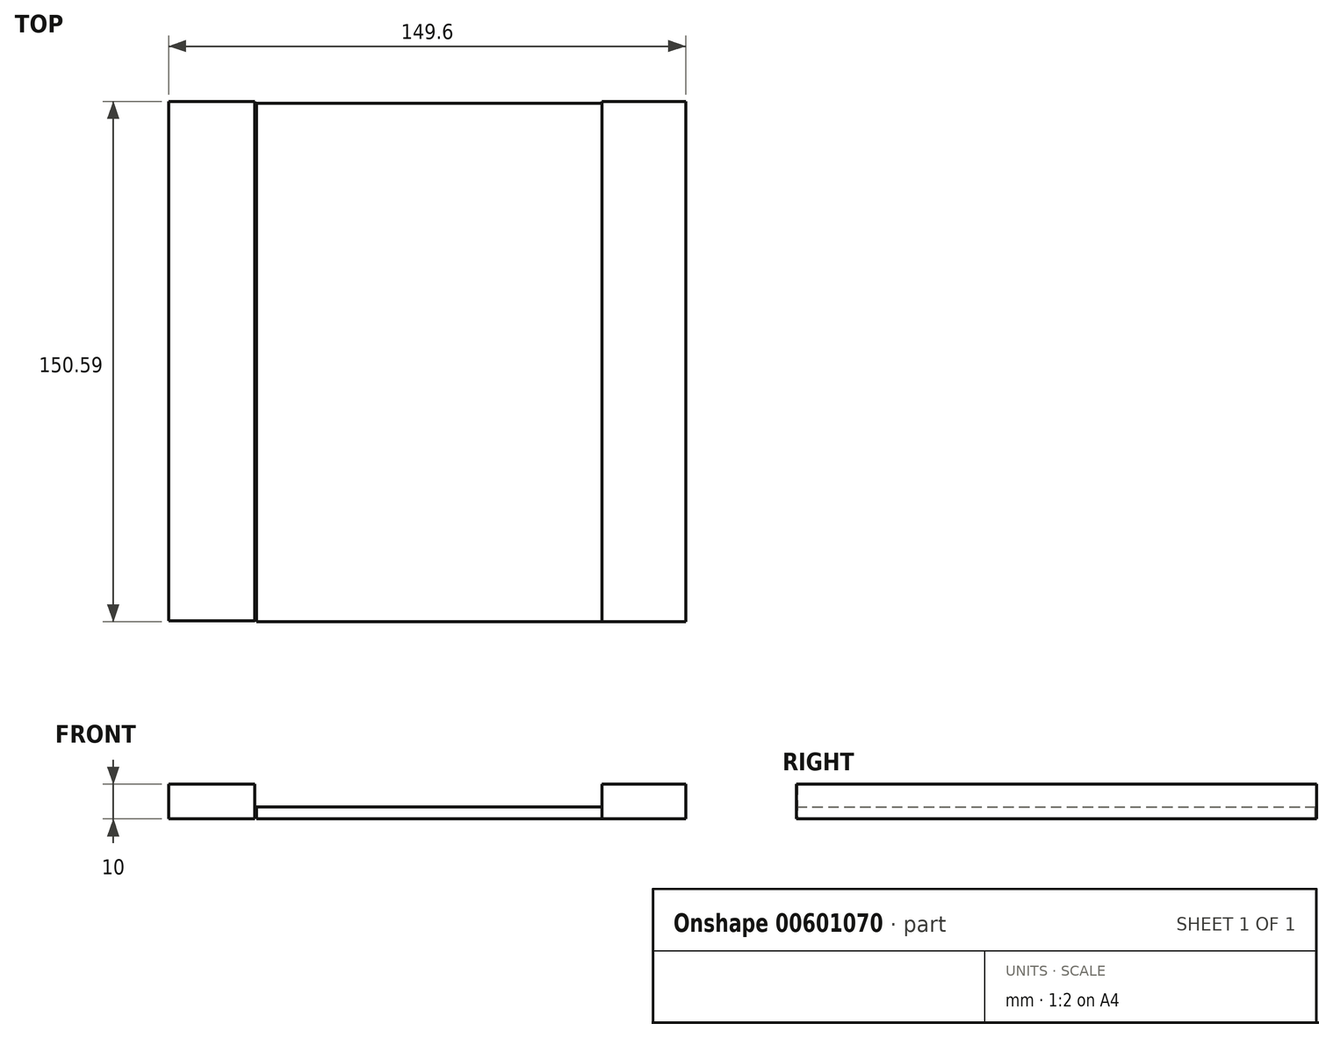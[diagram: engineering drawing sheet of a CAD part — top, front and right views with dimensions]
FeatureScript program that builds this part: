
annotation { "Feature Type Name" : "Feature", "Feature Type Description" : "" }
export const myFeature = defineFeature(function(context is Context, id is Id, definition is map)
    precondition{}
    {
        {
            var Q0;
            Q0=qCreatedBy(makeId("Top.planeOp"),FACE);
            var sketch = newSketch(context, id + "F0", { "sketchPlane" : qUnion([Q0])});
            skLineSegment(sketch, "E0.bottom", {"start": v(-48.63, 72.62) * mm, "end": v(51.37, 72.62) * mm});
            skLineSegment(sketch, "E0.top", {"start": v(-48.63, -77.38) * mm, "end": v(51.37, -77.38) * mm});
            skLineSegment(sketch, "E0.left", {"start": v(-48.63, 72.62) * mm, "end": v(-48.63, -77.38) * mm});
            skLineSegment(sketch, "E0.right", {"start": v(51.37, 72.62) * mm, "end": v(51.37, -77.38) * mm});
            skSolve(sketch);
        }
        {
            var Q0;
            Q0 = qSketchRegion(id + "F0", true);
            extrude(context, id + "F1", {"entities" : qUnion([Q0]), "depth" : 3.5 * mm, "offsetDistance" : 25 * mm});
        }
        {
            var Q0;
            Q0=qCreatedBy(makeId("Top.planeOp"),FACE);
            var sketch = newSketch(context, id + "F2", { "sketchPlane" : qUnion([Q0])});
            skLineSegment(sketch, "E1.bottom", {"start": v(-49.22, -77.14) * mm, "end": v(-74.1, -77.14) * mm});
            skLineSegment(sketch, "E1.top", {"start": v(-49.22, 73.12) * mm, "end": v(-74.1, 73.12) * mm});
            skLineSegment(sketch, "E1.left", {"start": v(-49.22, -77.14) * mm, "end": v(-49.22, 73.12) * mm});
            skLineSegment(sketch, "E1.right", {"start": v(-74.1, -77.14) * mm, "end": v(-74.1, 73.12) * mm});
            skLineSegment(sketch, "E2.bottom", {"start": v(51.28, 73.12) * mm, "end": v(75.5, 73.12) * mm});
            skLineSegment(sketch, "E2.top", {"start": v(51.28, -77.47) * mm, "end": v(75.5, -77.47) * mm});
            skLineSegment(sketch, "E2.left", {"start": v(51.28, 73.12) * mm, "end": v(51.28, -77.47) * mm});
            skLineSegment(sketch, "E2.right", {"start": v(75.5, 73.12) * mm, "end": v(75.5, -77.47) * mm});
            skSolve(sketch);
        }
        {
            var Q0;
            Q0=makeQuery(id+"F2.imprint","IMPRINT",FACE,{"disambiguationData":[TD([[makeQuery(id+"F2.imprint","IMPRINT",EDGE,{"derivedFrom":sQuery(id+"F2.wireOp",EDGE,"E1.bottom")}),-1.0]])]});
            var Q1;
            Q1=makeQuery(id+"F2.imprint","IMPRINT",FACE,{"disambiguationData":[TD([[makeQuery(id+"F2.imprint","IMPRINT",EDGE,{"derivedFrom":sQuery(id+"F2.wireOp",EDGE,"E2.bottom")}),-1.0]])]});
            extrude(context, id + "F3", {"entities" : qUnion([Q0, Q1]), "operationType" : NewBodyOperationType.ADD, "depth" : 10 * mm, "offsetDistance" : 25 * mm});
        }
    });
